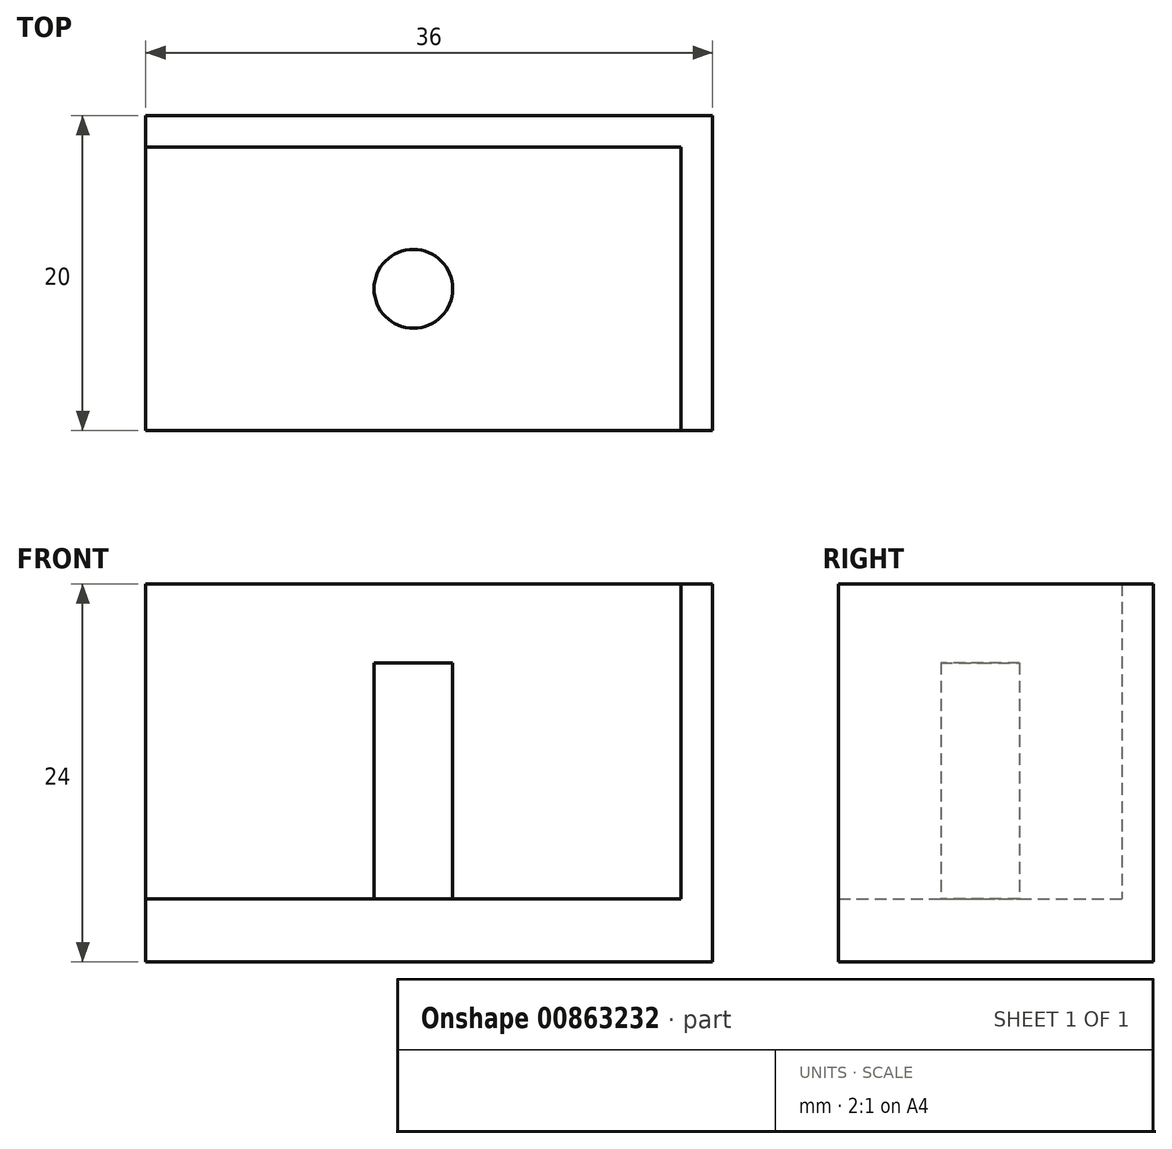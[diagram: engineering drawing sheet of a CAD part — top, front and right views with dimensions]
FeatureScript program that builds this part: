
annotation { "Feature Type Name" : "Feature", "Feature Type Description" : "" }
export const myFeature = defineFeature(function(context is Context, id is Id, definition is map)
    precondition{}
    {
        {
            var Q0;
            Q0=qCreatedBy(makeId("Top.planeOp"),FACE);
            var sketch = newSketch(context, id + "F0", { "sketchPlane" : qUnion([Q0])});
            skLineSegment(sketch, "E0.bottom", {"start": v(0, 0) * mm, "end": v(36, 0) * mm});
            skLineSegment(sketch, "E0.top", {"start": v(0, 20) * mm, "end": v(36, 20) * mm});
            skLineSegment(sketch, "E0.left", {"start": v(0, 0) * mm, "end": v(0, 20) * mm});
            skLineSegment(sketch, "E0.right", {"start": v(36, 0) * mm, "end": v(36, 20) * mm});
            skSolve(sketch);
        }
        {
            var Q0;
            Q0 = qSketchRegion(id + "F0", true);
            extrude(context, id + "F1", {"entities" : qUnion([Q0]), "depth" : 4 * mm, "offsetDistance" : 25 * mm});
        }
        {
            var Q0;
            Q0=makeQuery(id+"F1.opExtrude","CAP_FACE",FACE,{"disambiguationData":[OSD([sQuery(id+"F0.wireOp",EDGE,"E0.bottom"),sQuery(id+"F0.wireOp",EDGE,"E0.top"),sQuery(id+"F0.wireOp",EDGE,"E0.left"),sQuery(id+"F0.wireOp",EDGE,"E0.right")])],"isStart":false});
            var sketch = newSketch(context, id + "F2", { "sketchPlane" : qUnion([Q0])});
            skLineSegment(sketch, "E1", {"start": v(0, 20) * mm, "end": v(0, 18) * mm});
            skLineSegment(sketch, "E2", {"start": v(0, 18) * mm, "end": v(34, 18) * mm});
            skLineSegment(sketch, "E3", {"start": v(34, 18) * mm, "end": v(34, 0) * mm});
            skLineSegment(sketch, "E4", {"start": v(34, 0) * mm, "end": v(36, 0) * mm});
            skLineSegment(sketch, "E5", {"start": v(36, 0) * mm, "end": v(36, 20) * mm});
            skLineSegment(sketch, "E6", {"start": v(36, 20) * mm, "end": v(0, 20) * mm});
            skSolve(sketch);
        }
        {
            var Q0;
            Q0 = qSketchRegion(id + "F2", true);
            extrude(context, id + "F3", {"entities" : qUnion([Q0]), "operationType" : NewBodyOperationType.ADD, "depth" : 20 * mm, "offsetDistance" : 25 * mm});
        }
        {
            var Q0;
            Q0=makeQuery(id+"F1.opExtrude","CAP_FACE",FACE,{"disambiguationData":[OSD([sQuery(id+"F0.wireOp",EDGE,"E0.bottom"),sQuery(id+"F0.wireOp",EDGE,"E0.top"),sQuery(id+"F0.wireOp",EDGE,"E0.left"),sQuery(id+"F0.wireOp",EDGE,"E0.right")])],"isStart":false});
            var sketch = newSketch(context, id + "F4", { "sketchPlane" : qUnion([Q0])});
            skLineSegment(sketch, "E7", {"start": v(0, 18) * mm, "end": v(34, 0) * mm});
            skLineSegment(sketch, "E8", {"start": v(34, 18) * mm, "end": v(0, 0) * mm});
            skCircle(sketch, "E9", {"center": v(17, 9) * mm, "radius": 2.5 * mm});
            skSolve(sketch);
        }
        {
            var Q0;
            Q0 = qSketchRegion(id + "F4", true);
            extrude(context, id + "F5", {"entities" : qUnion([Q0]), "operationType" : NewBodyOperationType.ADD, "depth" : 15 * mm, "offsetDistance" : 25 * mm});
        }
    });
